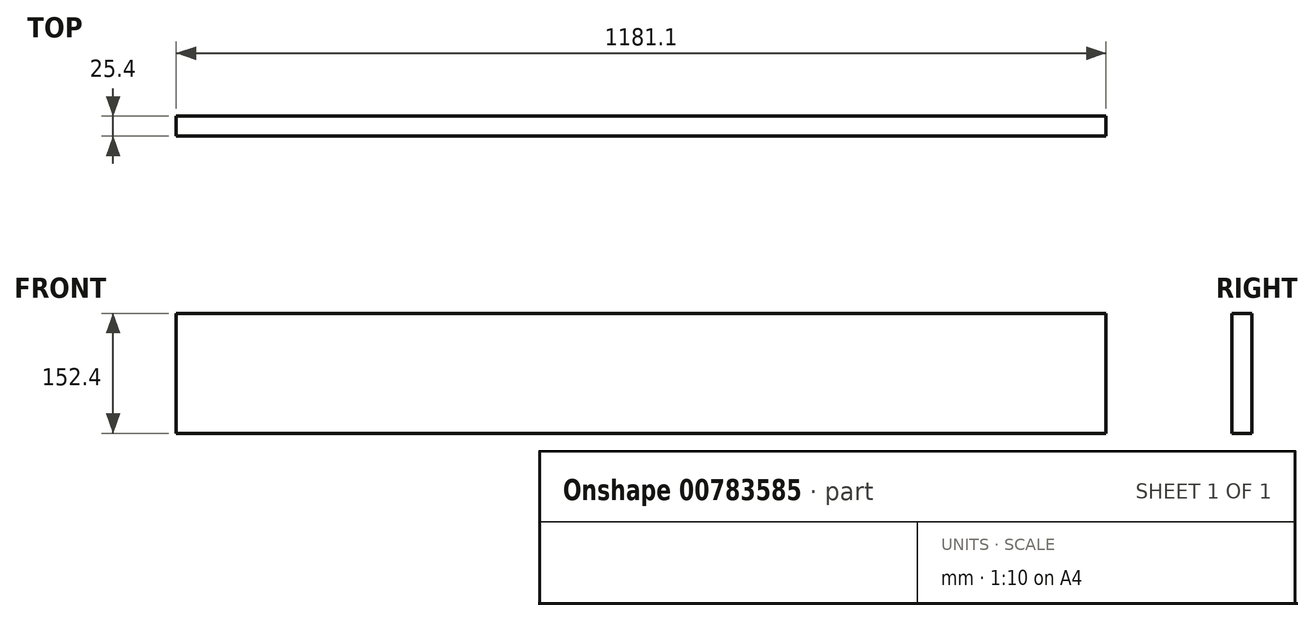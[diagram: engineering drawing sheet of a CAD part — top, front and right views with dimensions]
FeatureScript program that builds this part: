
annotation { "Feature Type Name" : "Feature", "Feature Type Description" : "" }
export const myFeature = defineFeature(function(context is Context, id is Id, definition is map)
    precondition{}
    {
        {
            var Q0;
            Q0=qCreatedBy(makeId("Front.planeOp"),FACE);
            var sketch = newSketch(context, id + "F0", { "sketchPlane" : qUnion([Q0])});
            skLineSegment(sketch, "E0.bottom", {"start": v(0, 0) * mm, "end": v(1181.1, 0) * mm});
            skLineSegment(sketch, "E0.top", {"start": v(0, 152.4) * mm, "end": v(1181.1, 152.4) * mm});
            skLineSegment(sketch, "E0.left", {"start": v(0, 0) * mm, "end": v(0, 152.4) * mm});
            skLineSegment(sketch, "E0.right", {"start": v(1181.1, 0) * mm, "end": v(1181.1, 152.4) * mm});
            skSolve(sketch);
        }
        {
            var Q0;
            Q0=makeQuery(id+"F0.imprint","IMPRINT",FACE,{"disambiguationData":[TD([[makeQuery(id+"F0.imprint","IMPRINT",EDGE,{"derivedFrom":sQuery(id+"F0.wireOp",EDGE,"E0.bottom")}),1.0]])]});
            extrude(context, id + "F1", {"entities" : qUnion([Q0]), "depth" : 25.4 * mm, "offsetDistance" : 25.4 * mm});
        }
    });
